# Revit family: TVM-H_DN20-25_RFA
name_source: partatom
category: Pipe Accessories
units: mm (PartAtom-declared; Revit-internal decimal feet)

## family parameters
Always vertical = Yes
Cut with Voids When Loaded = No
Part Type = Valve - Breaks Into
Round Connector Dimension = Use Diameter
Shared = No
Work Plane-Based = No

## types (2) — shared parameters
Connection = External Thread
D_B1 = 38 mm  [stored 0.124672 ft]
D_B2 = 25 mm  [stored 0.082021 ft]
D_B3 = 32 mm  [stored 0.104987 ft]
Description = Thermostatic Mixing Valve
H = 69 mm
H1 = 29 mm
H2 = 4 mm  [stored 0.0131234 ft]
H_B = 45 mm
H_B1 = 16 mm  [stored 0.0524934 ft]
H_B2 = 13 mm
IfcExportAs = IfcValveType
IfcExportType = TVM-H
L = 74 mm
L1 = 13 mm
LOD 200 = No
LOD 350 = Yes
Manufacturer = Danfoss
Max Differential Pressure = 5 bar
Max Medium Temperature = 70 °C
Max Static Pressure = 10 bar
Max Working Temperature = 100 °C
Min Medium Temperature = 30 °C
R_V1 = 16 mm  [stored 0.0524934 ft]
URL = https://store.danfoss.com
Valve Body Material = Danfoss Brass

## per-type parameters (varying)
| type | D | D_Thread | Kvs | L2 | Model | Model Type | Weight |
| TVM-H_DN20_003Z1120 | 20 mm  [stored 0.0656168 ft] | 33 mm | 1.9 m³/h | 2 mm  [stored 0.00656168 ft] | 003Z1120 | TVM-H_DN20 | 0.58 kg |
| TVM-H_DN25_003Z1127 | 25 mm  [stored 0.082021 ft] | 42 mm  [stored 0.137795 ft] | 3.0 m³/h | 3 mm  [stored 0.00984252 ft] | 003Z1127 | TVM-H_DN25 | 0.77 kg |

note: [stored X ft] marks values corroborated as IEEE doubles in the binary element streams (Revit-internal decimal feet)

## geometry (parser evidence)
native form markers: Sweep x4
no freeform markers — native parametric forms only
